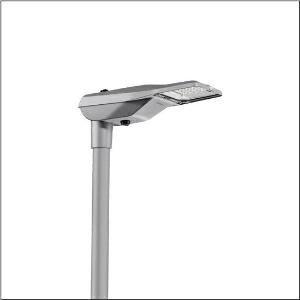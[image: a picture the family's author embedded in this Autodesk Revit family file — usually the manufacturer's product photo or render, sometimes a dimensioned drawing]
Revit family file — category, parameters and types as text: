
# Revit family: streetlight_sl_21_iq_micro___st1_0a_5xe1d41y08cb_9909
name_source: partatom
category: Lighting Fixtures
units: mm (PartAtom-declared; Revit-internal decimal feet)

## family parameters
Cut with Voids When Loaded = No
Host = Face
Light Source = No
Part Type = Normal
Room Calculation Point = No
Round Connector Dimension = Use Diameter
Shared = No

## types (1)
- --- (1 x LED, 2970 lm, 19.1 W, 4000K)
    Apparent Load = 19 VA
    CIE Flux Codes = 37 72 97 100 100
    Color Rendering = 70
    Color Temperature = 4000K
    Default Elevation = 1800 mm
    Description = Streetlight SL 21 iQ micro, mast luminaire, primary light control with lens, of PMMA, primary optical cover: cover, of toughened safety glass, transparent, light distribution: ST1.0a, light emission: direct distribution, primary light characteristic: asymmetric, installation type: post-top, side-entry, LED, High Power LED, rated luminous flux: 2.970lm, luminous efficacy: 156lm/W, light colour: 740, colour temperature: 4000K, control: presetting dimming logarithmic, Street-Remote, Auto-Match, Temp-Guard, Lumen-Switch, Night-Set, Smart-Wire, Light-Fading, Desk-Remote (wireless, voltage-free reading and setting of iQ features in the workshop via application-optimized NFC function/RFID function), optimised constant luminous flux control (CLO 2.0), mains connection: 220..240V, AC, 50/60Hz, start of lifetime: 19W, end of service life: 20W, reduction: 9W, luminaire housing, of diecast aluminium, powder-coated, Siteco® metallic grey (DB 702S), corrosivity category C5 mid according to DIN EN ISO 12944, please order mast flange separately, inclination adjustable: 0°, 5°, 10°, 15°, sealing non-destructively replaceable, multi-level sealing system, length: 528mm, width: 235mm, height: 110mm, mast flange for spigot size: 42mm (side-entry): 5XC10008XM4, 60/48mm (side-entry/post-top): 5XC10108XM2, 76/60mm (side-entry/post-top): 5XC10108XM1, Smart Interface below and above, protection rating (complete): IP66, insulation class (complete): insulation class II (safety insulation), certification: CE, ENEC, ENEC+, VDE, impact resistance: IK09, permissible operating ambient temperature for outdoor applications: -40..+50°C, standard-compliant lighting for roads and squares, packaging unit: 1 piece

Light Distribution: ST1.0a
    Height = 110 mm
    Lamp = 1 x LED
    Lamp Light Flux = 2970 lm
    Lamp Power = 19.1 W
    Lamp count = 1
    Length = 528 mm
    Luminous efficacy = 156 lm/W
    Manufacturer = Siteco
    ModVariant = No
    Model = 5XE1D41Y08CB
    Number of Poles = 1
    OnlyDefault = Yes
    Power Factor = 1
    Product Name = Streetlight SL 21 iQ micro | ST1.0a
    Product group = mast luminaire | pylon top
    ProductGroupID = 6100
    Protection Class = Protection class II
    Protection Degree = IP 66
    RLX_Detail_Level = 1
    RLX_Emergency_Light_Flux = 0 lm
    RLX_Emergency_Type = 0
    RLX_Emergency_Type_DB = No
    RlxData = <blob elided: 98885 chars, md5=8f8d66f8>
    Socket = socket
    Standby Power = 0 W
    System Light Flux = 2970 lm
    System Power = 19 W
    Type Comments = factory setting: luminous flux: 100 % | dim-lin: 254 | 387 mA
    Type Image = l_1007239.jpg
    URL = http://relux.com
    VarID = @adj_045343
    Voltage = 0 V
    Weight = 0.00 kg
    Width = 235 mm

## geometry (parser evidence)
native form markers: Blend x4, Sweep x10
no freeform markers — native parametric forms only
